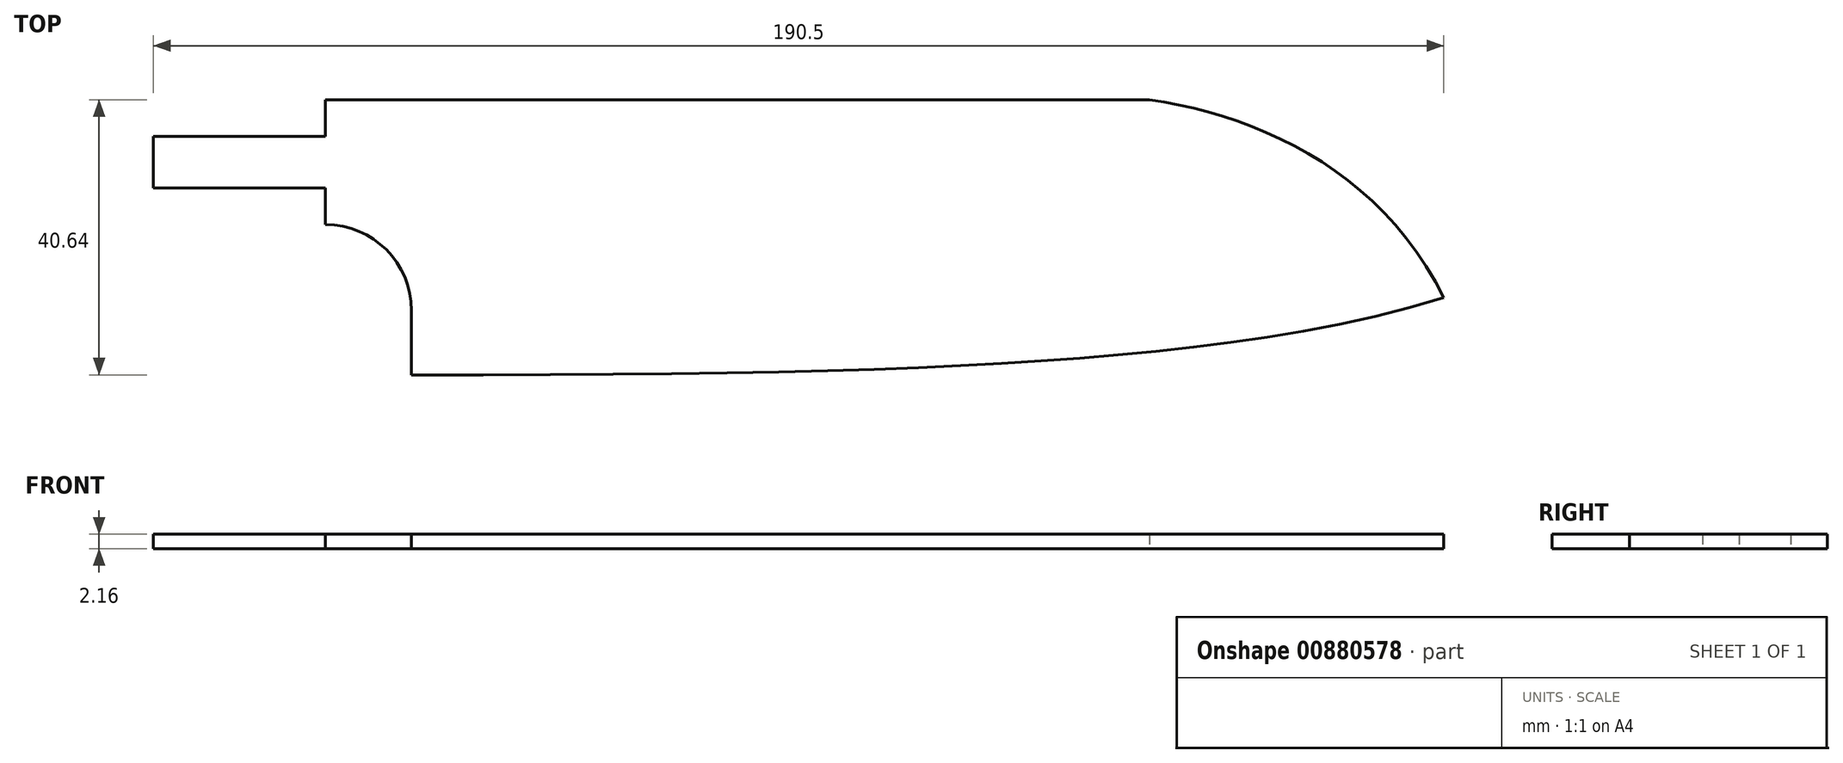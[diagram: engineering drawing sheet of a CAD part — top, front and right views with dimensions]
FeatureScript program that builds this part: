
annotation { "Feature Type Name" : "Feature", "Feature Type Description" : "" }
export const myFeature = defineFeature(function(context is Context, id is Id, definition is map)
    precondition{}
    {
        {
            var Q0;
            Q0=qCreatedBy(makeId("Top.planeOp"),FACE);
            var sketch = newSketch(context, id + "F0", { "sketchPlane" : qUnion([Q0])});
            skLineSegment(sketch, "E0.top", {"start": v(32.73, 20.32) * mm, "end": v(-76.2, 20.32) * mm});
            skLineSegment(sketch, "E0.right", {"start": v(-76.2, -20.32) * mm, "end": v(-76.2, -10.8) * mm});
            skPoint(sketch, "E0.middle", {"position": v(0, 0) * mm});
            skFitSpline(sketch, "E1", {"points": [v(32.73, 20.32) * mm, v(76.2, -8.9) * mm], "startDerivative": vector(49.4, -7.18) * mm, "endDerivative": vector(27.61, -55.77) * mm});
            skFitSpline(sketch, "E2", {"points": [v(-76.2, -20.32) * mm, v(24.5, -17.66) * mm, v(76.2, -8.9) * mm], "startDerivative": vector(251.92, 0) * mm, "endDerivative": vector(115.32, 35.64) * mm});
            skPoint(sketch, "E3.orphan", {"position": v(76.2, 20.32) * mm});
            skPoint(sketch, "E0.left.start.orphan", {"position": v(76.2, -20.32) * mm});
            skLineSegment(sketch, "E4.bottom", {"start": v(-76.2, 20.32) * mm, "end": v(-88.9, 20.32) * mm});
            skLineSegment(sketch, "E4.top", {"start": v(-88.9, 1.9) * mm, "end": v(-88.9, 1.9) * mm});
            skLineSegment(sketch, "E4.right", {"start": v(-88.9, 20.32) * mm, "end": v(-88.9, 14.92) * mm});
            skArc(sketch, "E5.filletArc", {"start": v(-76.2, -10.8) * mm, "mid": v(-79.92, -1.81) * mm, "end": v(-88.9, 1.9) * mm});
            skLineSegment(sketch, "E6.bottom", {"start": v(-114.3, 14.92) * mm, "end": v(-88.9, 14.92) * mm});
            skLineSegment(sketch, "E6.top", {"start": v(-114.3, 7.3) * mm, "end": v(-88.9, 7.3) * mm});
            skLineSegment(sketch, "E6.left", {"start": v(-114.3, 14.92) * mm, "end": v(-114.3, 7.3) * mm});
            skPoint(sketch, "E6.middle", {"position": v(-88.9, 11.11) * mm});
            skPoint(sketch, "E6.right.start.orphan", {"position": v(-63.5, 14.92) * mm});
            skLineSegment(sketch, "E7.trimOffspring", {"start": v(-88.9, 7.3) * mm, "end": v(-88.9, 1.9) * mm});
            skPoint(sketch, "E8.orphan", {"position": v(-63.5, 7.3) * mm});
            skSolve(sketch);
        }
        {
            var Q0;
            Q0 = qSketchRegion(id + "F0", true);
            extrude(context, id + "F1", {"entities" : qUnion([Q0]), "depth" : 2.16 * mm, "offsetDistance" : 25.4 * mm});
        }
    });
